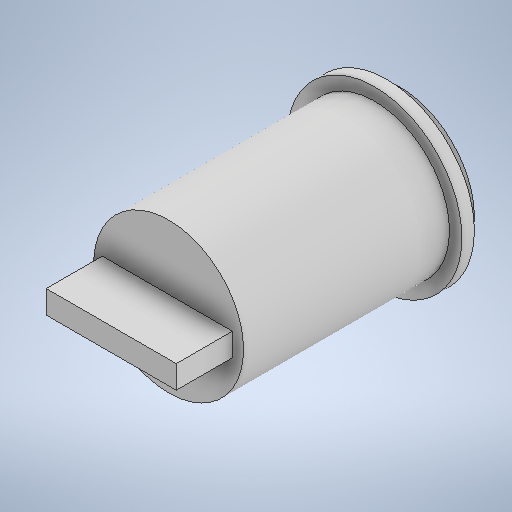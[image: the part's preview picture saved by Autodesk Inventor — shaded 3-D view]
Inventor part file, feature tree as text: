
AUTODESK INVENTOR PART (.ipt)
format: ipt  version: 2025.1 (Build 291241000, 241)  size: 259,584 bytes
history: native  units: mm
features: sketch x2, revolve x1, extrude x1
ambient origin geometry x8: Origin, YZ Plane, XZ Plane, XY Plane, X Axis, Y Axis, Z Axis, Center Point
bodies: Volumenkörper1 (feature_tree)
feature tree (4):
  revolve  "Umdrehung1"
  extrude  "Extrusion1"  Depth=16.5mm
  sketch  "Skizze1"  dims[d0=6.0mm d1=16.5mm]
  sketch  "Skizze2"  dims[d2=7.0mm d3=1.0mm d4=2.0mm d5=90.0deg d6=4.5mm d7=0.0mm]
